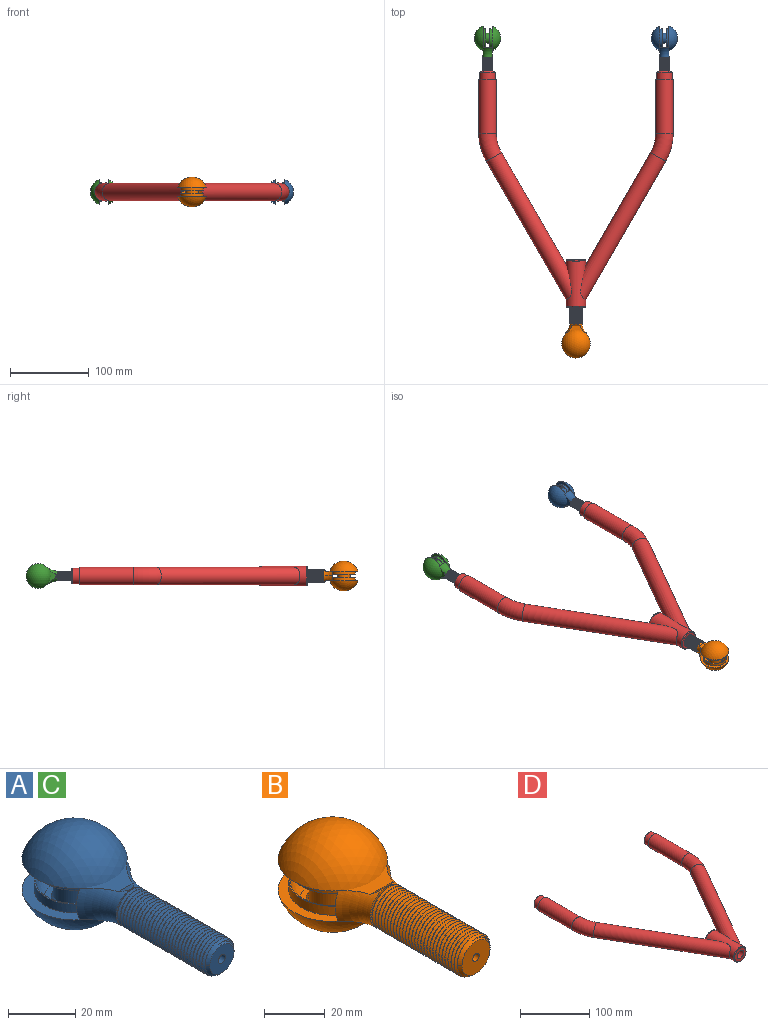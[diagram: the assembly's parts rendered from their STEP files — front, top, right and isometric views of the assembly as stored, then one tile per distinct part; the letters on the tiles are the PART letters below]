
ASSEMBLY  parts=4 mates=7
PART A: 88 faces, bbox 67.8x97.3x67.8 mm
  f0: cylinder r=12.03mm len=24.05mm, axis (0,0,1), area 245.9mm2, adj f1,f87
  f1: plane 30.08x30.08mm, normal (0,0,-1), area 28.6mm2, adj f0,f2
  f2: sphere r=11.91mm, area 421.7mm2, adj f1,f3
  f3: plane 17.75x17.75mm, normal (0,0,-1), area 94.1mm2, adj f2,f4
  f4: cone r=0mm half-angle=45deg, axis (0,0,-1), area 37.6mm2, adj f3,f5
  f5: cylinder r=6.35mm len=14.61mm, axis (0,0,1), area 582.7mm2, adj f4,f6
  f6: cone r=0mm half-angle=45deg, axis (0,0,1), area 37.6mm2, adj f5,f7
  f7: plane 37.19x37.19mm, normal (0,0,1), area 94.1mm2, adj f6,f8
  f8: sphere r=11.91mm, area 718.6mm2, adj f7,f9
  f9: plane 30.08x30.08mm, normal (0,0,1), area 28.6mm2, adj f8,f10
  f10: cylinder r=12.03mm len=24.05mm, axis (0,0,1), area 245.9mm2, adj f9,f11
  f11: plane 37.68x31.81mm, normal (0,0,1), area 376.1mm2, adj f10,f12,f84,f85,f86
  f12: torus R=22.32mm, axis (0,-1,0), area 180.4mm2, adj f11,f13,f15,f84,f86,f87
  f13: plane 6.9x3.09mm, normal (0,0.25,-0.97), area 9.3mm2, adj f12,f14,f87
  f14: torus R=22.32mm, axis (0,-1,0), area 90.2mm2, adj f13,f15,f84,f85,f87
  f15: plane 13.2x13.2mm, normal (0,-1,0), area 15.6mm2, adj f12,f14,f16,f82,f83,f85
  f16: bspline ~38.84x12.7mm, area 1026.5mm2, adj f15,f17,f18,f19,f20,f21,f22,f23
  f17: cylinder r=6.35mm len=12.7mm, axis (0,1,0), area 2.8mm2, adj f16,f18,f83,f85
  f18: cylinder r=6.35mm len=12.7mm, axis (0,1,0), area 3.2mm2, adj f16,f17,f19,f83
  f19: cylinder r=6.35mm len=12.7mm, axis (0,1,0), area 3.2mm2, adj f16,f18,f20,f83
  f20: cylinder r=6.35mm len=12.7mm, axis (0,1,0), area 3.2mm2, adj f16,f19,f21,f83
  f21: cylinder r=6.35mm len=12.7mm, axis (0,1,0), area 3.2mm2, adj f16,f20,f22,f83
  f22: cylinder r=6.35mm len=12.7mm, axis (0,1,0), area 3.2mm2, adj f16,f21,f23,f83
  f23: cylinder r=6.35mm len=12.7mm, axis (0,1,0), area 3.2mm2, adj f16,f22,f24,f83
  f24: cylinder r=6.35mm len=12.7mm, axis (0,1,0), area 3.2mm2, adj f16,f23,f25,f83
  f25: cylinder r=6.35mm len=12.7mm, axis (0,1,0), area 3.2mm2, adj f16,f24,f26,f83
  f26: cylinder r=6.35mm len=12.7mm, axis (0,1,0), area 3.2mm2, adj f16,f25,f27,f83
  f27: cylinder r=6.35mm len=12.7mm, axis (0,1,0), area 3.2mm2, adj f16,f26,f28,f83
  f28: cylinder r=6.35mm len=12.7mm, axis (0,1,0), area 3.2mm2, adj f16,f27,f29,f83
  f29: cylinder r=6.35mm len=12.7mm, axis (0,1,0), area 3.2mm2, adj f16,f28,f30,f83
  f30: cylinder r=6.35mm len=12.7mm, axis (0,1,0), area 3.2mm2, adj f16,f29,f31,f83
  f31: cylinder r=6.35mm len=12.7mm, axis (0,1,0), area 3.2mm2, adj f16,f30,f32,f83
  f32: cylinder r=6.35mm len=12.7mm, axis (0,1,0), area 3.2mm2, adj f16,f31,f33,f83
  f33: cylinder r=6.35mm len=12.7mm, axis (0,1,0), area 3.2mm2, adj f16,f32,f34,f83
  f34: cylinder r=6.35mm len=12.7mm, axis (0,1,0), area 3.2mm2, adj f16,f33,f35,f83
  f35: cylinder r=6.35mm len=12.7mm, axis (0,1,0), area 3.2mm2, adj f16,f34,f36,f83
  f36: cylinder r=6.35mm len=12.7mm, axis (0,1,0), area 3.2mm2, adj f16,f35,f37,f83
  f37: cylinder r=6.35mm len=12.7mm, axis (0,1,0), area 3.2mm2, adj f16,f36,f38,f83
  f38: cylinder r=6.35mm len=12.7mm, axis (0,1,0), area 3.2mm2, adj f16,f37,f39,f83
  f39: cylinder r=6.35mm len=12.7mm, axis (0,1,0), area 3.2mm2, adj f16,f38,f40,f83
  f40: cylinder r=6.35mm len=12.7mm, axis (0,1,0), area 3.2mm2, adj f16,f39,f41,f83
  f41: cylinder r=6.35mm len=12.7mm, axis (0,1,0), area 3.2mm2, adj f16,f40,f42,f83
  f42: cylinder r=6.35mm len=12.7mm, axis (0,1,0), area 3.2mm2, adj f16,f41,f43,f83
  f43: cylinder r=6.35mm len=12.7mm, axis (0,1,0), area 3.2mm2, adj f16,f42,f44,f83
  f44: cylinder r=6.35mm len=12.7mm, axis (0,1,0), area 3.2mm2, adj f16,f43,f45,f83
  f45: cylinder r=6.35mm len=12.7mm, axis (0,1,0), area 3.2mm2, adj f16,f44,f46,f83
  f46: cylinder r=6.35mm len=12.7mm, axis (0,1,0), area 3.2mm2, adj f16,f45,f47,f83
  f47: cylinder r=6.35mm len=12.7mm, axis (0,1,0), area 3.2mm2, adj f16,f46,f48,f83
  f48: cylinder r=6.35mm len=12.7mm, axis (0,1,0), area 3.2mm2, adj f16,f47,f49,f83
  f49: cylinder r=6.35mm len=12.7mm, axis (0,1,0), area 3.2mm2, adj f16,f48,f50,f83
  f50: cylinder r=6.35mm len=12.7mm, axis (0,1,0), area 3.2mm2, adj f16,f49,f51,f83
  f51: cylinder r=6.35mm len=12.7mm, axis (0,1,0), area 3.2mm2, adj f16,f50,f52,f83
  f52: cylinder r=6.35mm len=12.7mm, axis (0,1,0), area 3.2mm2, adj f16,f51,f53,f83
  f53: cylinder r=6.35mm len=12.7mm, axis (0,1,0), area 3.2mm2, adj f16,f52,f54,f83
  f54: cylinder r=6.35mm len=12.7mm, axis (0,1,0), area 3.2mm2, adj f16,f53,f55,f83
  f55: cylinder r=6.35mm len=12.7mm, axis (0,1,0), area 3.2mm2, adj f16,f54,f56,f83
  f56: cylinder r=6.35mm len=12.7mm, axis (0,1,0), area 3.2mm2, adj f16,f55,f57,f83
  f57: cylinder r=6.35mm len=12.7mm, axis (0,1,0), area 3.2mm2, adj f16,f56,f58,f83
  f58: cylinder r=6.35mm len=12.7mm, axis (0,1,0), area 3.2mm2, adj f16,f57,f59,f83
  f59: cylinder r=6.35mm len=12.7mm, axis (0,1,0), area 3.2mm2, adj f16,f58,f60,f83
  f60: cylinder r=6.35mm len=12.7mm, axis (0,1,0), area 3.2mm2, adj f16,f59,f61,f83
  f61: cylinder r=6.35mm len=12.7mm, axis (0,1,0), area 3.2mm2, adj f16,f60,f62,f83
  f62: cylinder r=6.35mm len=12.7mm, axis (0,1,0), area 3.2mm2, adj f16,f61,f63,f83
  f63: cylinder r=6.35mm len=12.7mm, axis (0,1,0), area 3.2mm2, adj f16,f62,f64,f83
  f64: cylinder r=6.35mm len=12.7mm, axis (0,1,0), area 3.2mm2, adj f16,f63,f65,f83
  f65: cylinder r=6.35mm len=12.7mm, axis (0,1,0), area 3.2mm2, adj f16,f64,f66,f83
  f66: cylinder r=6.35mm len=12.7mm, axis (0,1,0), area 3.2mm2, adj f16,f65,f67,f83
  f67: cylinder r=6.35mm len=12.7mm, axis (0,1,0), area 3.2mm2, adj f16,f66,f68,f83
  f68: cylinder r=6.35mm len=12.7mm, axis (0,1,0), area 3.2mm2, adj f16,f67,f69,f83
  f69: cylinder r=6.35mm len=12.7mm, axis (0,1,0), area 3.2mm2, adj f16,f68,f70,f83
  f70: cylinder r=6.35mm len=12.7mm, axis (0,1,0), area 3.2mm2, adj f16,f69,f71,f83
  f71: cylinder r=6.35mm len=12.7mm, axis (0,1,0), area 3.2mm2, adj f16,f70,f72,f83
  f72: cylinder r=6.35mm len=12.7mm, axis (0,1,0), area 3.2mm2, adj f16,f71,f73,f83
  f73: cylinder r=6.35mm len=12.7mm, axis (0,1,0), area 3.2mm2, adj f16,f72,f74,f76,f83
  f74: cylinder r=6.35mm len=12.7mm, axis (0,1,0), area 3.2mm2, adj f73,f75,f76,f83
  f75: cylinder r=6.35mm len=4.49mm, axis (0,1,0), area 0.4mm2, adj f74,f76,f81
  f76: bspline ~14.55x14.53mm, area 18.3mm2, adj f73,f74,f75,f77,f81
  f77: cone r=0mm half-angle=45deg, axis (0,1,0), area 18.6mm2, adj f76,f78,f81
  f78: plane 10.16x10.16mm, normal (0,-1,0), area 74mm2, adj f77,f79,f81
  f79: cylinder r=1.5mm len=15mm, axis (0,-1,0), area 141.4mm2, adj f78,f80
  f80: plane 3x3mm, normal (0,-1,0), area 7.1mm2, adj f79
  f81: cone r=0mm half-angle=45deg, axis (0,1,0), area 23.7mm2, adj f16,f75,f76,f77,f78,f82,f83
  f82: cylinder r=5.53mm len=37.66mm, axis (0,1,0), area 165.1mm2, adj f15,f16,f81,f83
  f83: bspline ~38.26x12.7mm, area 1045.6mm2, adj f15,f17,f18,f19,f20,f21,f22,f23
  f84: sphere r=16.67mm, area 2557.4mm2, adj f11,f12,f14,f85,f87
  f85: torus R=22.32mm, axis (0,-1,0), area 90.2mm2, adj f11,f14,f15,f17,f84,f86
  f86: plane 6.9x3.09mm, normal (0,0.25,0.97), area 9.3mm2, adj f11,f12,f85
  f87: plane 37.68x31.81mm, normal (0,0,-1), area 376.3mm2, adj f0,f12,f13,f14,f84
PART B: 86 faces, bbox 74.1x108.1x74.1 mm
  f0: cylinder r=14.43mm len=28.86mm, axis (0,0,1), area 331.1mm2, adj f1,f2
  f1: plane 41.2x36.29mm, normal (0,0,-1), area 441.4mm2, adj f0,f3,f4,f5,f6
  f2: plane 35.07x35.07mm, normal (0,0,-1), area 32.5mm2, adj f0,f7
  f3: sphere r=19.05mm, area 3418.5mm2, adj f1,f4,f6,f8,f9
  f4: torus R=23.47mm, axis (0,-1,0), area 92.7mm2, adj f1,f3,f5,f8,f10,f11
  f5: plane 11.68x3.5mm, normal (0,0.59,-0.81), area 21.6mm2, adj f1,f4,f6
  f6: torus R=23.47mm, axis (0,-1,0), area 185.4mm2, adj f1,f3,f5,f9,f10,f12
  f7: sphere r=14.29mm, area 649.9mm2, adj f2,f13
  f8: torus R=23.47mm, axis (0,-1,0), area 92.7mm2, adj f3,f4,f9,f10,f12
  f9: plane 41.19x36.28mm, normal (0,0,1), area 441.4mm2, adj f3,f6,f8,f12,f14
  f10: plane 16.47x16.47mm, normal (0,-1,0), area 21.8mm2, adj f4,f6,f8,f15,f16,f17
  f11: cylinder r=7.94mm len=7.85mm, axis (0,1,0), area 1.4mm2, adj f4,f15,f17,f18
  f12: plane 11.68x3.5mm, normal (0,0.59,0.81), area 21.6mm2, adj f6,f8,f9
  f13: plane 21.3x21.3mm, normal (0,0,-1), area 116.8mm2, adj f7,f19
  f14: cylinder r=14.43mm len=28.86mm, axis (0,0,1), area 331.1mm2, adj f9,f20
  f15: bspline ~41.48x15.88mm, area 1421.3mm2, adj f10,f11,f16,f18,f21,f22,f23,f24
  f16: cylinder r=7.02mm len=40.78mm, axis (0,-1,0), area 224.7mm2, adj f10,f15,f17,f21
  f17: bspline ~41.84x15.87mm, area 1394.1mm2, adj f10,f11,f16,f18,f21,f22,f23,f24
  f18: cylinder r=7.94mm len=15.88mm, axis (0,1,0), area 4.4mm2, adj f11,f15,f17,f22
  f19: cone r=0mm half-angle=45deg, axis (0,0,-1), area 58.8mm2, adj f13,f79
  f20: plane 35.07x35.07mm, normal (0,0,1), area 32.5mm2, adj f14,f80
  f21: cone r=0mm half-angle=45deg, axis (0,1,0), area 33.4mm2, adj f15,f16,f17,f77,f78,f81
  f22: cylinder r=7.94mm len=15.88mm, axis (0,1,0), area 4.4mm2, adj f15,f17,f18,f23
  f23: cylinder r=7.94mm len=15.88mm, axis (0,1,0), area 4.4mm2, adj f15,f17,f22,f24
  f24: cylinder r=7.94mm len=15.88mm, axis (0,1,0), area 4.4mm2, adj f15,f17,f23,f25
  f25: cylinder r=7.94mm len=15.88mm, axis (0,1,0), area 4.4mm2, adj f15,f17,f24,f26
  f26: cylinder r=7.94mm len=15.88mm, axis (0,1,0), area 4.4mm2, adj f15,f17,f25,f27
  f27: cylinder r=7.94mm len=15.88mm, axis (0,1,0), area 4.4mm2, adj f15,f17,f26,f28
  f28: cylinder r=7.94mm len=15.88mm, axis (0,1,0), area 4.4mm2, adj f15,f17,f27,f29
  f29: cylinder r=7.94mm len=15.88mm, axis (0,1,0), area 4.4mm2, adj f15,f17,f28,f30
  f30: cylinder r=7.94mm len=15.88mm, axis (0,1,0), area 4.4mm2, adj f15,f17,f29,f31
  f31: cylinder r=7.94mm len=15.88mm, axis (0,1,0), area 4.4mm2, adj f15,f17,f30,f32
  f32: cylinder r=7.94mm len=15.88mm, axis (0,1,0), area 4.4mm2, adj f15,f17,f31,f33
  f33: cylinder r=7.94mm len=15.88mm, axis (0,1,0), area 4.4mm2, adj f15,f17,f32,f34
  f34: cylinder r=7.94mm len=15.88mm, axis (0,1,0), area 4.4mm2, adj f15,f17,f33,f35
  f35: cylinder r=7.94mm len=15.88mm, axis (0,1,0), area 4.4mm2, adj f15,f17,f34,f36
  f36: cylinder r=7.94mm len=15.88mm, axis (0,1,0), area 4.4mm2, adj f15,f17,f35,f37
  f37: cylinder r=7.94mm len=15.88mm, axis (0,1,0), area 4.4mm2, adj f15,f17,f36,f38
  f38: cylinder r=7.94mm len=15.88mm, axis (0,1,0), area 4.4mm2, adj f15,f17,f37,f39
  f39: cylinder r=7.94mm len=15.88mm, axis (0,1,0), area 4.4mm2, adj f15,f17,f38,f40
  f40: cylinder r=7.94mm len=15.88mm, axis (0,1,0), area 4.4mm2, adj f15,f17,f39,f41
  f41: cylinder r=7.94mm len=15.88mm, axis (0,1,0), area 4.4mm2, adj f15,f17,f40,f42
  f42: cylinder r=7.94mm len=15.88mm, axis (0,1,0), area 4.4mm2, adj f15,f17,f41,f43
  f43: cylinder r=7.94mm len=15.88mm, axis (0,1,0), area 4.4mm2, adj f15,f17,f42,f44
  f44: cylinder r=7.94mm len=15.88mm, axis (0,1,0), area 4.4mm2, adj f15,f17,f43,f45
  f45: cylinder r=7.94mm len=15.88mm, axis (0,1,0), area 4.4mm2, adj f15,f17,f44,f46
  f46: cylinder r=7.94mm len=15.88mm, axis (0,1,0), area 4.4mm2, adj f15,f17,f45,f47
  f47: cylinder r=7.94mm len=15.88mm, axis (0,1,0), area 4.4mm2, adj f15,f17,f46,f48
  f48: cylinder r=7.94mm len=15.88mm, axis (0,1,0), area 4.4mm2, adj f15,f17,f47,f49
  f49: cylinder r=7.94mm len=15.88mm, axis (0,1,0), area 4.4mm2, adj f15,f17,f48,f50
  f50: cylinder r=7.94mm len=15.88mm, axis (0,1,0), area 4.4mm2, adj f15,f17,f49,f51
  f51: cylinder r=7.94mm len=15.88mm, axis (0,1,0), area 4.4mm2, adj f15,f17,f50,f52
  f52: cylinder r=7.94mm len=15.88mm, axis (0,1,0), area 4.4mm2, adj f15,f17,f51,f53
  f53: cylinder r=7.94mm len=15.88mm, axis (0,1,0), area 4.4mm2, adj f15,f17,f52,f54
  f54: cylinder r=7.94mm len=15.88mm, axis (0,1,0), area 4.4mm2, adj f15,f17,f53,f55
  f55: cylinder r=7.94mm len=15.88mm, axis (0,1,0), area 4.4mm2, adj f15,f17,f54,f56
  f56: cylinder r=7.94mm len=15.88mm, axis (0,1,0), area 4.4mm2, adj f15,f17,f55,f57
  f57: cylinder r=7.94mm len=15.88mm, axis (0,1,0), area 4.4mm2, adj f15,f17,f56,f58
  f58: cylinder r=7.94mm len=15.88mm, axis (0,1,0), area 4.4mm2, adj f15,f17,f57,f59
  f59: cylinder r=7.94mm len=15.88mm, axis (0,1,0), area 4.4mm2, adj f15,f17,f58,f60
  f60: cylinder r=7.94mm len=15.88mm, axis (0,1,0), area 4.4mm2, adj f15,f17,f59,f61
  f61: cylinder r=7.94mm len=15.88mm, axis (0,1,0), area 4.4mm2, adj f15,f17,f60,f62
  f62: cylinder r=7.94mm len=15.88mm, axis (0,1,0), area 4.4mm2, adj f15,f17,f61,f63
  f63: cylinder r=7.94mm len=15.88mm, axis (0,1,0), area 4.4mm2, adj f15,f17,f62,f64
  f64: cylinder r=7.94mm len=15.88mm, axis (0,1,0), area 4.4mm2, adj f15,f17,f63,f65
  f65: cylinder r=7.94mm len=15.88mm, axis (0,1,0), area 4.4mm2, adj f15,f17,f64,f66
  f66: cylinder r=7.94mm len=15.88mm, axis (0,1,0), area 4.4mm2, adj f15,f17,f65,f67
  f67: cylinder r=7.94mm len=15.88mm, axis (0,1,0), area 4.4mm2, adj f15,f17,f66,f68
  f68: cylinder r=7.94mm len=15.88mm, axis (0,1,0), area 4.4mm2, adj f15,f17,f67,f69
  f69: cylinder r=7.94mm len=15.88mm, axis (0,1,0), area 4.4mm2, adj f15,f17,f68,f70
  f70: cylinder r=7.94mm len=15.88mm, axis (0,1,0), area 4.4mm2, adj f15,f17,f69,f71
  f71: cylinder r=7.94mm len=15.88mm, axis (0,1,0), area 4.4mm2, adj f15,f17,f70,f72
  f72: cylinder r=7.94mm len=15.88mm, axis (0,1,0), area 4.4mm2, adj f15,f17,f71,f73
  f73: cylinder r=7.94mm len=15.88mm, axis (0,1,0), area 4.4mm2, adj f15,f17,f72,f74
  f74: cylinder r=7.94mm len=15.88mm, axis (0,1,0), area 4.4mm2, adj f15,f17,f73,f75
  f75: cylinder r=7.94mm len=15.88mm, axis (0,1,0), area 4.4mm2, adj f15,f17,f74,f76
  f76: cylinder r=7.94mm len=15.88mm, axis (0,1,0), area 4.4mm2, adj f15,f17,f75,f78
  f77: cone r=0mm half-angle=45deg, axis (0,1,0), area 26.4mm2, adj f17,f21,f81
  f78: cylinder r=7.94mm len=5.61mm, axis (0,1,0), area 0.6mm2, adj f17,f21,f76
  f79: cylinder r=7.94mm len=17.46mm, axis (0,0,1), area 870.9mm2, adj f19,f82
  f80: sphere r=14.29mm, area 1077.4mm2, adj f20,f83
  f81: plane 13.05x13.05mm, normal (0,-1,0), area 126.7mm2, adj f21,f77,f84
  f82: cone r=0mm half-angle=45deg, axis (0,0,1), area 58.8mm2, adj f79,f83
  f83: plane 44.63x44.63mm, normal (0,0,1), area 116.8mm2, adj f80,f82
  f84: cylinder r=1.5mm len=20mm, axis (0,-1,0), area 188.5mm2, adj f81,f85
  f85: plane 3x3mm, normal (0,-1,0), area 7.1mm2, adj f84
PART C: same geometry as A
PART D: 34 faces, bbox 258.9x300x25 mm
  f0: cylinder r=12.5mm len=58mm, axis (0,-1,0), area 2754.5mm2, adj f1,f17,f22,f30,f32,f33
  f1: cone r=12.5mm half-angle=45deg, axis (0,-1,0), area 97.3mm2, adj f0,f19,f32
  f2: plane 18.23x18.23mm, normal (0,-1,0), area 156.8mm2, adj f6,f7
  f3: cylinder r=12.5mm len=36.47mm, axis (0,-1,0), area 566.9mm2, adj f4
  f4: cylinder r=9.11mm len=182.21mm, axis (-0.5,-0.87,0), area 10753.4mm2, adj f3,f5
  f5: torus R=60mm, axis (0,0,-1), area 1797.6mm2, adj f4,f6
  f6: cylinder r=9.11mm len=58.93mm, axis (0,-1,0), area 3374.3mm2, adj f2,f5
  f7: cylinder r=5.75mm len=20mm, axis (0,1,0), area 723.1mm2, adj f2,f24
  f8: plane 18.23x18.23mm, normal (0,-1,0), area 156.8mm2, adj f12,f13
  f9: cylinder r=12.5mm len=36.47mm, axis (0,-1,0), area 566.9mm2, adj f10
  f10: cylinder r=9.11mm len=182.21mm, axis (0.5,-0.87,0), area 10753.4mm2, adj f9,f11
  f11: torus R=60mm, axis (0,0,-1), area 1797.6mm2, adj f10,f12
  f12: cylinder r=9.11mm len=58.93mm, axis (0,-1,0), area 3374.3mm2, adj f8,f11
  f13: cylinder r=5.75mm len=20mm, axis (0,1,0), area 723.1mm2, adj f8,f27
  f14: plane 22.23x22.23mm, normal (0,1,0), area 73.8mm2, adj f15,f25
  f15: cylinder r=11.11mm len=68.93mm, axis (0,-1,0), area 4813.1mm2, adj f14,f16
  f16: torus R=60mm, axis (0,0,-1), area 2192.2mm2, adj f15,f17
  f17: cylinder r=11.11mm len=187.23mm, axis (-0.5,-0.87,0), area 13278.9mm2, adj f0,f16
  f18: plane 23x23mm, normal (0,-1,0), area 272.5mm2, adj f30,f31
  f19: plane 23x23mm, normal (0,1,0), area 272.5mm2, adj f1,f31
  f20: cylinder r=11.11mm len=68.93mm, axis (0,-1,0), area 4813.1mm2, adj f21,f23
  f21: torus R=60mm, axis (0,0,-1), area 2192.2mm2, adj f20,f22
  f22: cylinder r=11.11mm len=187.23mm, axis (0.5,-0.87,0), area 13278.9mm2, adj f0,f21
  f23: plane 22.23x22.23mm, normal (0,1,0), area 73.8mm2, adj f20,f26
  f24: plane 18x18mm, normal (0,1,0), area 150.4mm2, adj f7,f29
  f25: cylinder r=10mm len=20mm, axis (0,1,0), area 565.5mm2, adj f14,f29
  f26: cylinder r=10mm len=20mm, axis (0,1,0), area 565.5mm2, adj f23,f28
  f27: plane 18x18mm, normal (0,1,0), area 150.4mm2, adj f13,f28
  f28: cone r=10mm half-angle=45deg, axis (0,-1,0), area 84.4mm2, adj f26,f27
  f29: cone r=10mm half-angle=45deg, axis (0,-1,0), area 84.4mm2, adj f24,f25
  f30: cone r=11.5mm half-angle=45deg, axis (0,1,0), area 106.6mm2, adj f0,f18
  f31: cylinder r=6.75mm len=60mm, axis (0,-1,0), area 2543.3mm2, adj f18,f19
  f32: plane 9.81x2.01mm, normal (0,0,1), area 16.3mm2, adj f0,f1,f33
  f33: plane 9.8x1mm, normal (0,1,0), area 6.6mm2, adj f0,f32
PLACE A rot(axis=(0,1,0),90deg) t=(112.5,28.1,0)mm
PLACE B rot(axis=(0,0,1),180deg) t=(0,-311.28,0)mm
PLACE C rot(axis=(0,1,0),90deg) t=(-112.5,28.1,0)mm
PLACE D at identity fixed
MATE planar D.f25 <-> A.f17  axis (0,1,0) through (112.5,10,0)mm
MATE cylindrical A.f79 <-> D.f7  axis (0,-1,0) through (112.5,-2.5,0)mm
MATE cylindrical A.f0 <-> C.f0  axis (1,0,0) through (119.8,51.91,0)mm
MATE parallel B.f0 <-> D.f32  axis (0,0,1) through (0,-336.68,9.52)mm
MATE cylindrical B.f84 <-> D.f31  axis (0,1,0) through (0,-280,0)mm
MATE planar D.f0 <-> B.f84  axis (0,-1,0) through (0,-290,0)mm
MATE cylindrical C.f79 <-> D.f13  axis (0,-1,0) through (-112.5,-2.5,0)mm
